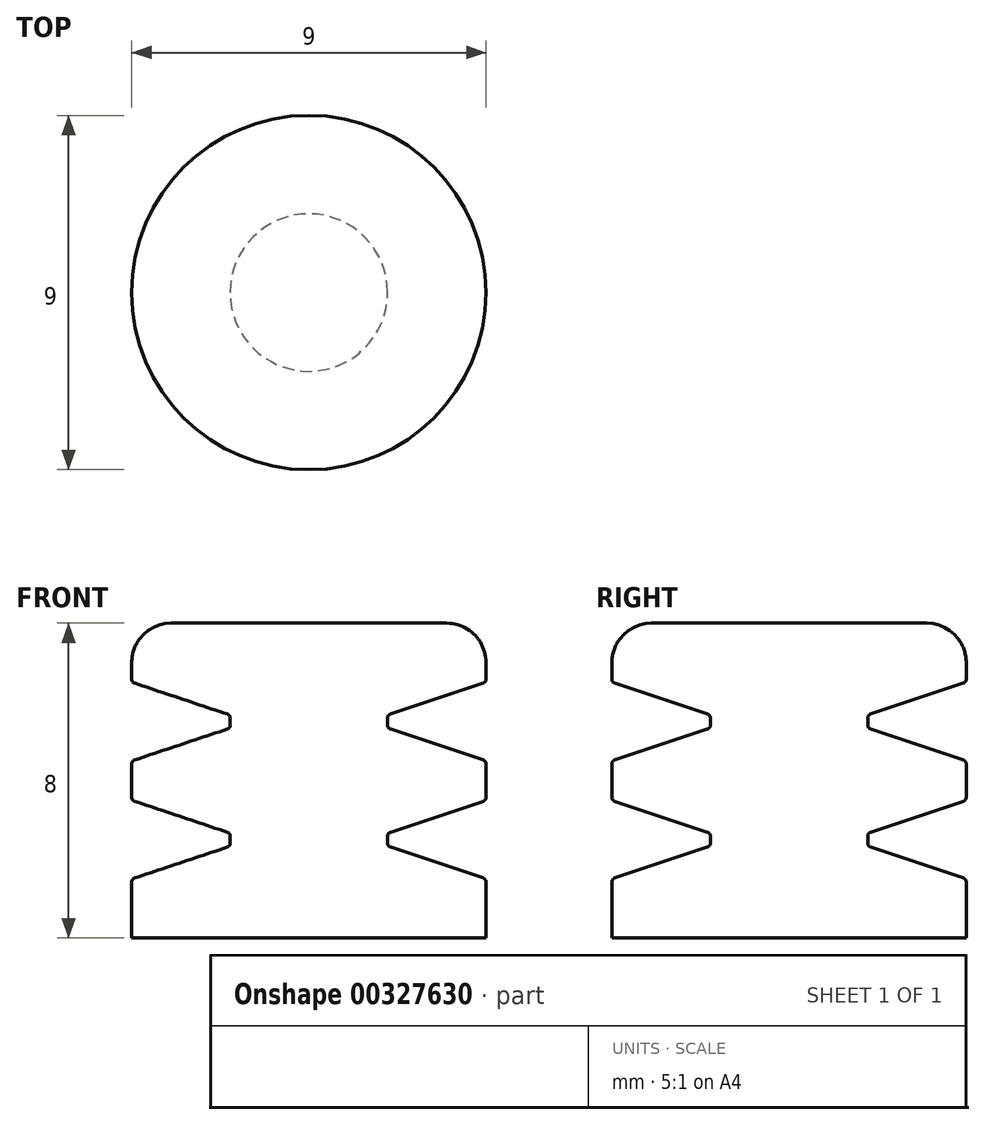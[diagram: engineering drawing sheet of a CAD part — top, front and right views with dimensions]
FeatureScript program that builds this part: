
annotation { "Feature Type Name" : "Feature", "Feature Type Description" : "" }
export const myFeature = defineFeature(function(context is Context, id is Id, definition is map)
    precondition{}
    {
        {
            var Q0;
            Q0=qCreatedBy(makeId("Front.planeOp"),FACE);
            var sketch = newSketch(context, id + "F0", { "sketchPlane" : qUnion([Q0])});
            skLineSegment(sketch, "E0", {"start": v(0, 0) * mm, "end": v(4.5, 0) * mm});
            skLineSegment(sketch, "E1", {"start": v(4.5, 0) * mm, "end": v(4.5, 0.5) * mm});
            skLineSegment(sketch, "E2", {"start": v(0, 0) * mm, "end": v(0, 1.5) * mm});
            skLineSegment(sketch, "E3", {"start": v(0, 1.5) * mm, "end": v(1.5, 1.5) * mm});
            skLineSegment(sketch, "E4", {"start": v(4.5, 0.5) * mm, "end": v(1.5, 1.5) * mm});
            skLineSegment(sketch, "E5", {"start": v(1.5, 1.5) * mm, "end": v(2, 1.5) * mm});
            skLineSegment(sketch, "E6", {"start": v(2, 1.33) * mm, "end": v(2, 1.5) * mm});
            skSolve(sketch);
        }
        {
            var Q0;
            Q0=makeQuery(id+"F0.imprint","IMPRINT",FACE,{"disambiguationData":[TD([[makeQuery(id+"F0.imprint","IMPRINT",EDGE,{"derivedFrom":sQuery(id+"F0.wireOp",EDGE,"E0")}),1.0]])]});
            var Q1;
            {var subQ0=sQuery(id+"F0.wireOp",EDGE,"E5");Q1=makeQuery(id+"F0.imprint","IMPRINT",FACE,{"disambiguationData":[TD([[makeQuery(id+"F0.imprint","IMPRINT",EDGE,{"derivedFrom":subQ0}),-1.0]])]});}
            var Q2;
            Q2=sQuery(id+"F0.wireOp",EDGE,"E2");
            revolve(context, id + "F1", {"entities" : qUnion([Q0, Q1]), "axis" : qUnion([Q2]), "revolveType" : RevolveType.FULL});
        }
        {
            var Q0;
            Q0=makeQuery(id+"F1.opRevolve","SWEPT_EDGE",EDGE,{"disambiguationData":[OSD([sQuery(id+"F0.wireOp",EDGE,"E4"),sQuery(id+"F0.wireOp",EDGE,"E6")])]});
            var Q1;
            Q1=makeQuery(id+"F1.opRevolve","SWEPT_EDGE",EDGE,{"disambiguationData":[OSD([sQuery(id+"F0.wireOp",EDGE,"E1"),sQuery(id+"F0.wireOp",EDGE,"E4")])]});
            fillet(context, id + "F2", {"entities" : qUnion([Q0, Q1]), "radius" : 0.1 * mm, "tangentPropagation" : true, "allowEdgeOverflow" : false});
        }
        {
            var Q0;
            Q0=makeQuery(id+"F1.opRevolve","SWEPT_BODY",BODY,{"disambiguationData":[OSD([sQuery(id+"F0.wireOp",EDGE,"E0"),sQuery(id+"F0.wireOp",EDGE,"E1"),sQuery(id+"F0.wireOp",EDGE,"E2"),sQuery(id+"F0.wireOp",EDGE,"E3"),sQuery(id+"F0.wireOp",EDGE,"E4"),sQuery(id+"F0.wireOp",EDGE,"E5"),sQuery(id+"F0.wireOp",EDGE,"E6")])]});
            var Q1;
            Q1=makeQuery(id+"F1.opRevolve","SWEPT_FACE",FACE,{"disambiguationData":[OSD([sQuery(id+"F0.wireOp",EDGE,"E3"),sQuery(id+"F0.wireOp",EDGE,"E5")])]});
            mirror(context, id + "F3", {"operationType" : NewBodyOperationType.ADD, "entities" : qUnion([Q0]), "mirrorPlane" : qUnion([Q1])});
        }
        {
            var Q0;
            Q0=makeQuery(id+"F1.opRevolve","SWEPT_BODY",BODY,{"disambiguationData":[OSD([sQuery(id+"F0.wireOp",EDGE,"E0"),sQuery(id+"F0.wireOp",EDGE,"E1"),sQuery(id+"F0.wireOp",EDGE,"E2"),sQuery(id+"F0.wireOp",EDGE,"E3"),sQuery(id+"F0.wireOp",EDGE,"E4"),sQuery(id+"F0.wireOp",EDGE,"E5"),sQuery(id+"F0.wireOp",EDGE,"E6")])]});
            var Q1;
            Q1=makeQuery(id+"F3.opPattern","COPY",FACE,{"derivedFrom":makeQuery(id+"F1.opRevolve","SWEPT_FACE",FACE,{"disambiguationData":[OSD([sQuery(id+"F0.wireOp",EDGE,"E0")])]}),"instanceName":"1"});
            mirror(context, id + "F4", {"operationType" : NewBodyOperationType.ADD, "entities" : qUnion([Q0]), "mirrorPlane" : qUnion([Q1])});
        }
        {
            var Q0;
            Q0=makeQuery(id+"F4.opPattern","COPY",FACE,{"derivedFrom":makeQuery(id+"F1.opRevolve","SWEPT_FACE",FACE,{"disambiguationData":[OSD([sQuery(id+"F0.wireOp",EDGE,"E0")])]}),"instanceName":"1"});
            extrude(context, id + "F5", {"entities" : qUnion([Q0]), "operationType" : NewBodyOperationType.ADD, "depth" : 1 * mm});
        }
        {
            var Q0;
            Q0=makeQuery(id+"F1.opRevolve","SWEPT_FACE",FACE,{"disambiguationData":[OSD([sQuery(id+"F0.wireOp",EDGE,"E0")])]});
            extrude(context, id + "F6", {"entities" : qUnion([Q0]), "operationType" : NewBodyOperationType.ADD, "depth" : 1 * mm});
        }
        {
            var Q0;
            Q0=makeQuery(id+"F5.opExtrude","CAP_EDGE",EDGE,{"disambiguationData":[OSD([sQuery(id+"F0.wireOp",EDGE,"E0"),sQuery(id+"F0.wireOp",EDGE,"E1")])],"isStart":false});
            fillet(context, id + "F7", {"entities" : qUnion([Q0]), "radius" : 1 * mm, "tangentPropagation" : true, "allowEdgeOverflow" : false});
        }
    });
